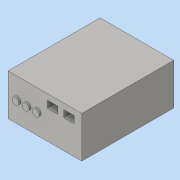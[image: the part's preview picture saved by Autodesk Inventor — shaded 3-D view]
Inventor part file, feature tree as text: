
AUTODESK INVENTOR PART (.ipt)
format: ipt  version: 2016 (Build 200138000, 138)  size: 100,864 bytes
history: native  units: in
note: dims shown in document units (in); Inventor stores cm internally (conversion verified against a paired STEP export)
features: extrude x3, sketch x3
ambient origin geometry x8: Origin, YZ Plane, XZ Plane, XY Plane, X Axis, Y Axis, Z Axis, Center Point
bodies: Solid1 (feature_tree)
feature tree (6):
  extrude  "WR-LEN"  Depth=2.25in
  extrude  "sfp ports"  Depth=0.375in
  extrude  "Extrusion3"  Depth=0.5in TaperAngle=0.0deg
  sketch  "Sketch1"  dims[d0=4.0in d1=2.25in]
  sketch  "Sketch2"  dims[d2=5.0in d3=0.0in d4=0.375in]
  sketch  "Sketch3"  dims[d5=0.5625in d6=0.5in d7=0.0in d9=0.379in d10=0.5in d11=1.125in d12=1.1811in d14=0.55in d15=0.3937in d17=1.0in d19=0.1in d20=0.0in]
